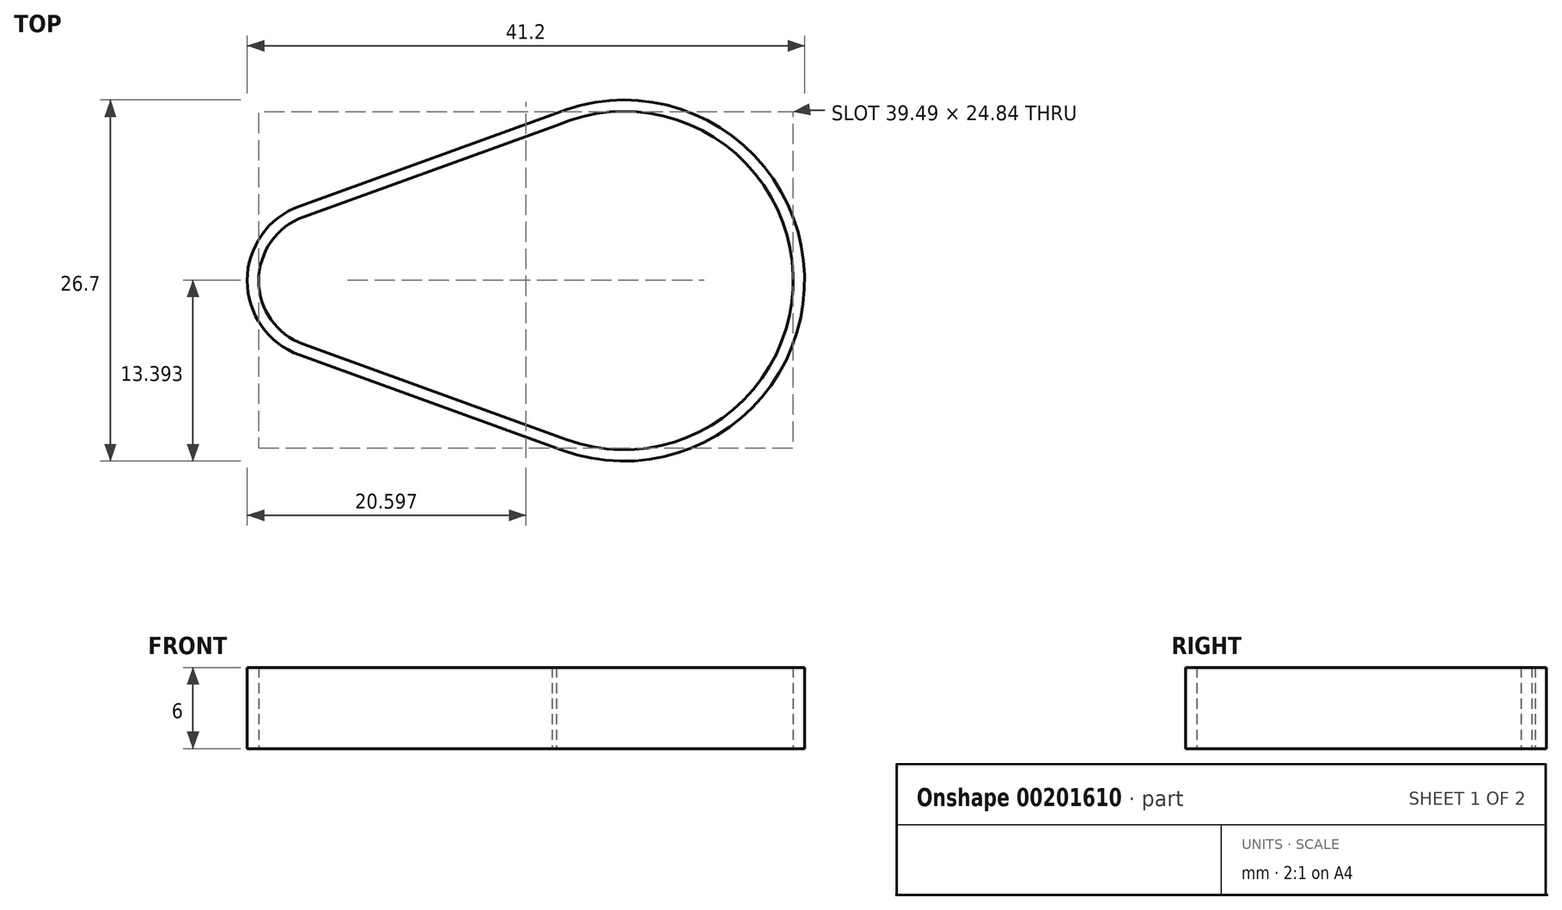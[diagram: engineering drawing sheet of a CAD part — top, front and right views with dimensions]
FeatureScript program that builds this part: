
annotation { "Feature Type Name" : "Feature", "Feature Type Description" : "" }
export const myFeature = defineFeature(function(context is Context, id is Id, definition is map)
    precondition{}
    {
        {
            var Q0;
            Q0=qCreatedBy(makeId("Top.planeOp"),FACE);
            var sketch = newSketch(context, id + "F0", { "sketchPlane" : qUnion([Q0])});
            skArc(sketch, "E0", {"start": v(-1.7, 4.7) * mm, "mid": v(-5, 0) * mm, "end": v(-1.7, -4.7) * mm});
            skArc(sketch, "E1", {"start": v(17.74, -11.75) * mm, "mid": v(34.5, 0.4) * mm, "end": v(17, 11.46) * mm});
            skLineSegment(sketch, "E2", {"start": v(-1.7, 4.7) * mm, "end": v(17, 11.46) * mm});
            skLineSegment(sketch, "E3", {"start": v(-1.7, -4.7) * mm, "end": v(17.74, -11.75) * mm});
            skLineSegment(sketch, "E4.0", {"start": v(-2, -5.5) * mm, "end": v(17.45, -12.55) * mm});
            skArc(sketch, "E4.1", {"start": v(-1.99, 5.5) * mm, "mid": v(-5.85, 0) * mm, "end": v(-2, -5.5) * mm});
            skLineSegment(sketch, "E4.2", {"start": v(-1.99, 5.5) * mm, "end": v(16.68, 12.25) * mm});
            skArc(sketch, "E4.3", {"start": v(17.45, -12.55) * mm, "mid": v(35.34, 0.41) * mm, "end": v(16.68, 12.25) * mm});
            skSolve(sketch);
        }
        {
            var Q0;
            Q0=makeQuery(id+"F0.imprint","IMPRINT",FACE,{"disambiguationData":[TD([[makeQuery(id+"F0.imprint","IMPRINT",EDGE,{"derivedFrom":sQuery(id+"F0.wireOp",EDGE,"E0")}),-1.0]])]});
            extrude(context, id + "F1", {"entities" : qUnion([Q0]), "depth" : 6 * mm});
        }
    });
